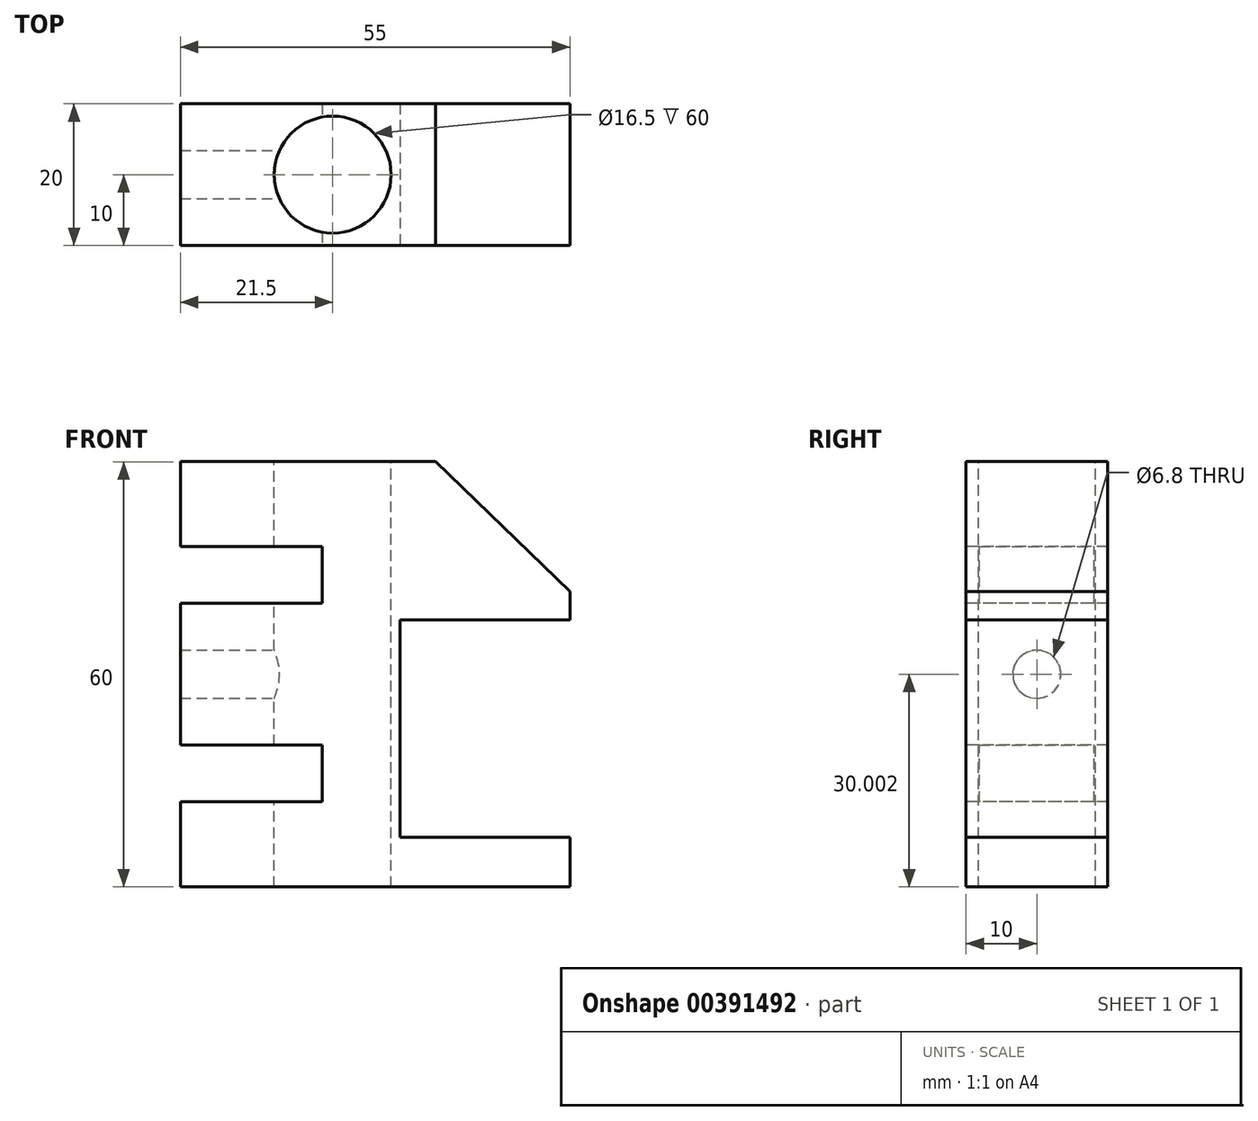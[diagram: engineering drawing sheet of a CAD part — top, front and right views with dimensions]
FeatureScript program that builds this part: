
annotation { "Feature Type Name" : "Feature", "Feature Type Description" : "" }
export const myFeature = defineFeature(function(context is Context, id is Id, definition is map)
    precondition{}
    {
        {
            var Q0;
            Q0=qCreatedBy(makeId("Front.planeOp"),FACE);
            var sketch = newSketch(context, id + "F0", { "sketchPlane" : qUnion([Q0])});
            skLineSegment(sketch, "E0", {"start": v(-36, -45.89) * mm, "end": v(19, -45.89) * mm});
            skLineSegment(sketch, "E1", {"start": v(19, -45.89) * mm, "end": v(19, -38.89) * mm});
            skLineSegment(sketch, "E2", {"start": v(19, -38.89) * mm, "end": v(-5, -38.89) * mm});
            skLineSegment(sketch, "E3", {"start": v(-5, -38.89) * mm, "end": v(-5, -8.19) * mm});
            skLineSegment(sketch, "E4", {"start": v(-5, -8.19) * mm, "end": v(19, -8.19) * mm});
            skLineSegment(sketch, "E5", {"start": v(19, -8.19) * mm, "end": v(19, -4.19) * mm});
            skLineSegment(sketch, "E6", {"start": v(19, -4.19) * mm, "end": v(0, 14.11) * mm});
            skLineSegment(sketch, "E7", {"start": v(0, 14.11) * mm, "end": v(-36, 14.11) * mm});
            skLineSegment(sketch, "E8", {"start": v(-36, 14.11) * mm, "end": v(-36, 2.11) * mm});
            skLineSegment(sketch, "E9", {"start": v(-36, 2.11) * mm, "end": v(-16, 2.11) * mm});
            skLineSegment(sketch, "E10", {"start": v(-16, 2.11) * mm, "end": v(-16, -5.89) * mm});
            skLineSegment(sketch, "E11", {"start": v(-16, -5.89) * mm, "end": v(-36, -5.89) * mm});
            skLineSegment(sketch, "E12", {"start": v(-36, -5.89) * mm, "end": v(-36, -25.89) * mm});
            skLineSegment(sketch, "E13", {"start": v(-36, -25.89) * mm, "end": v(-16, -25.89) * mm});
            skLineSegment(sketch, "E14", {"start": v(-16, -25.89) * mm, "end": v(-16, -33.89) * mm});
            skLineSegment(sketch, "E15", {"start": v(-16, -33.89) * mm, "end": v(-36, -33.89) * mm});
            skLineSegment(sketch, "E16", {"start": v(-36, -33.89) * mm, "end": v(-36, -45.89) * mm});
            skSolve(sketch);
        }
        {
            var Q0;
            Q0=makeQuery(id+"F0.imprint","IMPRINT",FACE,{"disambiguationData":[TD([[makeQuery(id+"F0.imprint","IMPRINT",EDGE,{"derivedFrom":sQuery(id+"F0.wireOp",EDGE,"E0")}),1.0]])]});
            extrude(context, id + "F1", {"entities" : qUnion([Q0]), "oppositeDirection" : true, "depth" : 20 * mm});
        }
        {
            var Q0;
            Q0=makeQuery(id+"F1.opExtrude","SWEPT_FACE",FACE,{"disambiguationData":[OSD([sQuery(id+"F0.wireOp",EDGE,"E7")])]});
            var sketch = newSketch(context, id + "F2", { "sketchPlane" : qUnion([Q0])});
            skLineSegment(sketch, "E17", {"start": v(-36, 10) * mm, "end": v(0, 10) * mm, "construction": true});
            skLineSegment(sketch, "E18.0", {"start": v(-14.5, 20) * mm, "end": v(-14.5, 0) * mm, "construction": true});
            skCircle(sketch, "E19", {"center": v(-14.5, 10) * mm, "radius": 8.25 * mm});
            skSolve(sketch);
        }
        {
            var Q0;
            Q0=makeQuery(id+"F2.imprint","IMPRINT",FACE,{"disambiguationData":[TD([[makeQuery(id+"F2.imprint","IMPRINT",EDGE,{"derivedFrom":sQuery(id+"F2.wireOp",EDGE,"E19")}),1.0]])]});
            extrude(context, id + "F3", {"entities" : qUnion([Q0]), "operationType" : NewBodyOperationType.REMOVE, "endBound" : BoundingType.THROUGH_ALL, "oppositeDirection" : true, "depth" : 25 * mm});
        }
        {
            var Q0;
            Q0=makeQuery(id+"F1.opExtrude","SWEPT_FACE",FACE,{"disambiguationData":[OSD([sQuery(id+"F0.wireOp",EDGE,"E12")])]});
            var sketch = newSketch(context, id + "F4", { "sketchPlane" : qUnion([Q0])});
            skLineSegment(sketch, "E20", {"start": v(-10, -5.89) * mm, "end": v(-10, -25.89) * mm, "construction": true});
            skLineSegment(sketch, "E21", {"start": v(-20, -15.89) * mm, "end": v(0, -15.89) * mm, "construction": true});
            skCircle(sketch, "E22", {"center": v(-10, -15.89) * mm, "radius": 3.4 * mm});
            skSolve(sketch);
        }
        {
            var Q0;
            Q0=sQuery(id+"F4.wireOp",VERTEX,"E22.center");
            var Q1;
            Q1=makeQuery(id+"F1.opExtrude","SWEPT_BODY",BODY,{"disambiguationData":[OSD([sQuery(id+"F0.wireOp",EDGE,"E0"),sQuery(id+"F0.wireOp",EDGE,"E1"),sQuery(id+"F0.wireOp",EDGE,"E2"),sQuery(id+"F0.wireOp",EDGE,"E3"),sQuery(id+"F0.wireOp",EDGE,"E4"),sQuery(id+"F0.wireOp",EDGE,"E5"),sQuery(id+"F0.wireOp",EDGE,"E6"),sQuery(id+"F0.wireOp",EDGE,"E7"),sQuery(id+"F0.wireOp",EDGE,"E8"),sQuery(id+"F0.wireOp",EDGE,"E9"),sQuery(id+"F0.wireOp",EDGE,"E10"),sQuery(id+"F0.wireOp",EDGE,"E11"),sQuery(id+"F0.wireOp",EDGE,"E12"),sQuery(id+"F0.wireOp",EDGE,"E13"),sQuery(id+"F0.wireOp",EDGE,"E14"),sQuery(id+"F0.wireOp",EDGE,"E15"),sQuery(id+"F0.wireOp",EDGE,"E16")])]});
            hole(context, id + "F5", {"style" : HoleStyle.SIMPLE, "endStyle" : HoleEndStyle.BLIND, "holeDiameter" : 6.8 * mm, "holeDepth" : 20 * mm, "isTappedThrough" : true, "tappedDepth" : 12 * mm, "tapClearance" : 3, "locations" : qUnion([Q0]), "scope" : qUnion([Q1]), "startStyle" : HoleStartStyle.SKETCH});
        }
    });
